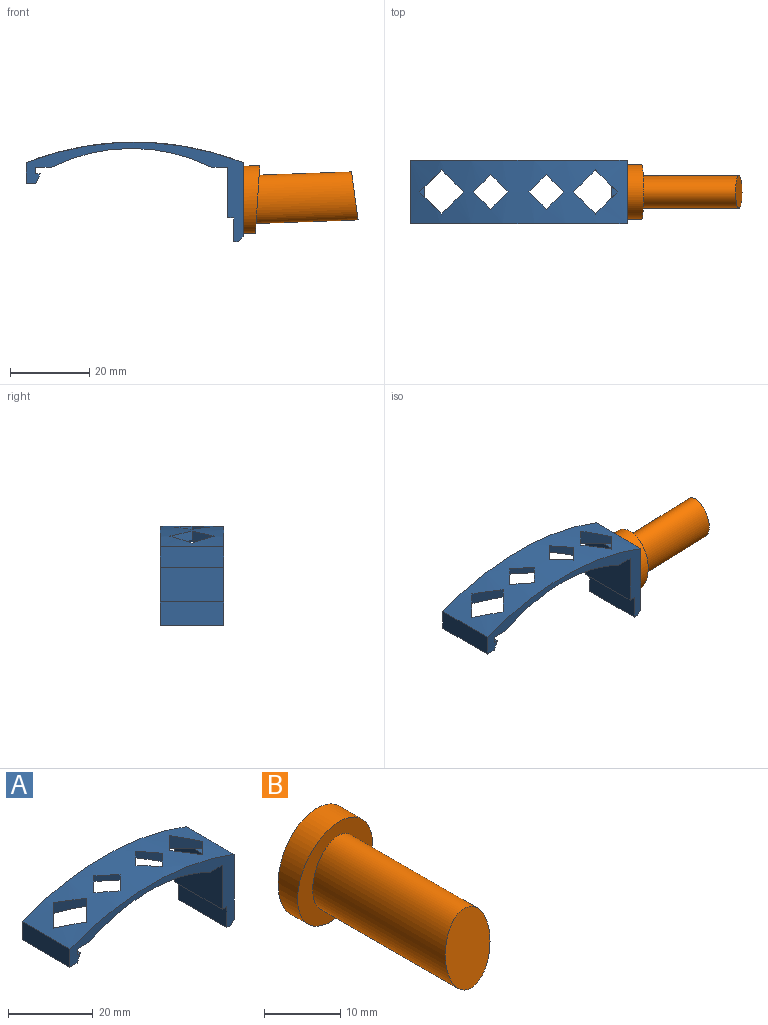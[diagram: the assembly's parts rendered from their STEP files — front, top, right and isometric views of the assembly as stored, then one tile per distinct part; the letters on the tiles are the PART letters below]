
ASSEMBLY  parts=2 mates=1
PART A: 36 faces, bbox 54.9x16x25.2 mm
  f0: plane 6.5x4mm, normal (0,0,-1), area 18mm2, adj f5,f6,f17,f28
  f1: plane 6.5x4mm, normal (0,0,-1), area 18mm2, adj f5,f6,f16,f27
  f2: plane 8x4mm, normal (0,0,-1), area 24mm2, adj f5,f15,f16,f31
  f3: plane 8x4mm, normal (0,0,-1), area 24mm2, adj f5,f15,f17,f34
  f4: cylinder r=75.05mm len=54.9mm, axis (0,1,0), area 691.5mm2, adj f10,f11,f16,f17,f18,f19,f20,f21
  f5: cylinder r=45.33mm len=40.6mm, axis (0,1,0), area 508.8mm2, adj f0,f1,f2,f3,f16,f17,f18,f19
  f6: plane 16x12.8mm, normal (-1,0,0), area 204.8mm2, adj f0,f1,f7,f16,f17,f30
  f7: plane 16x1.5mm, normal (0,0,-1), area 24mm2, adj f6,f8,f16,f17
  f8: plane 16x6mm, normal (-1,0,0), area 96mm2, adj f7,f9,f16,f17
  f9: plane 16x1.2mm, normal (0,0,-1), area 19.2mm2, adj f8,f16,f17,f35
  f10: plane 18.8x16mm, normal (1,0,0), area 300.8mm2, adj f4,f16,f17,f35
  f11: plane 16x5.25mm, normal (-1,0,0), area 84mm2, adj f4,f12,f16,f17
  f12: plane 16x2.4mm, normal (0,0,-1), area 38.4mm2, adj f11,f13,f16,f17
  f13: plane 16x2.4mm, normal (0.89,0,-0.45), area 42.9mm2, adj f12,f14,f16,f17
  f14: plane 16x1.2mm, normal (0,0,1), area 19.2mm2, adj f13,f15,f16,f17
  f15: plane 16x1.65mm, normal (1,0,0), area 26.4mm2, adj f2,f3,f14,f16,f17
  f16: plane 54.9x25.2mm, normal (0,-1,0), area 201mm2, adj f1,f2,f4,f5,f6,f7,f8,f9
  f17: plane 54.9x25.2mm, normal (0,1,0), area 201mm2, adj f0,f3,f4,f5,f6,f7,f8,f9
  f18: plane 4.41x4.41mm, normal (-0.71,0.71,0), area 10.2mm2, adj f4,f5,f19,f21
  f19: plane 4.41x4.41mm, normal (-0.71,-0.71,0), area 10.2mm2, adj f4,f5,f18,f20
  f20: plane 4.41x4.41mm, normal (0.71,-0.71,0), area 11.4mm2, adj f4,f5,f19,f21
  f21: plane 4.41x4.41mm, normal (0.71,0.71,0), area 11.4mm2, adj f4,f5,f18,f20
  f22: plane 4.41x4.41mm, normal (-0.71,0.71,0), area 13.4mm2, adj f4,f5,f23,f25
  f23: plane 4.41x4.41mm, normal (-0.71,-0.71,0), area 13.4mm2, adj f4,f5,f22,f24
  f24: plane 4.41x4.41mm, normal (0.71,-0.71,0), area 11.2mm2, adj f4,f5,f23,f25
  f25: plane 4.41x4.41mm, normal (0.71,0.71,0), area 11.2mm2, adj f4,f5,f22,f24
  f26: plane 5.6x5.6mm, normal (0.71,0.71,0), area 25.5mm2, adj f4,f5,f27,f29
  f27: plane 5.6x5.6mm, normal (-0.71,0.71,0), area 23.8mm2, adj f1,f4,f5,f26,f28,f30
  f28: plane 5.6x5.6mm, normal (-0.71,-0.71,0), area 23.8mm2, adj f0,f4,f5,f27,f29,f30
  f29: plane 5.6x5.6mm, normal (0.71,-0.71,0), area 25.5mm2, adj f4,f5,f26,f28
  f30: plane 3x1.5mm, normal (0,0,1), area 2.3mm2, adj f6,f27,f28
  f31: plane 5.61x5.61mm, normal (0.71,0.71,0), area 22.9mm2, adj f2,f4,f5,f32,f34
  f32: plane 5.6x5.6mm, normal (-0.71,0.71,0), area 20.8mm2, adj f4,f5,f31,f33
  f33: plane 5.6x5.6mm, normal (-0.71,-0.71,0), area 20.8mm2, adj f4,f5,f32,f34
  f34: plane 5.61x5.61mm, normal (0.71,-0.71,0), area 22.9mm2, adj f3,f4,f5,f31,f33
  f35: plane 16x1.2mm, normal (0.71,0,-0.71), area 27.2mm2, adj f9,f10,f16,f17
PART B: 5 faces, bbox 13.8x29.2x17 mm
  f0: extruded ~25.82x12.2mm, area 795.9mm2, adj f1,f2
  f1: plane 12.2x8.2mm, normal (0,-1,0.1), area 79mm2, adj f0
  f2: plane 17x13.81mm, normal (0,-1,-0.1), area 106.3mm2, adj f0,f3
  f3: extruded ~17x13.8mm, area 178.5mm2, adj f2,f4
  f4: plane 17x13.81mm, normal (0,1,0.03), area 184.5mm2, adj f3
PLACE A t=(-21.06,0.13,2.96)mm
PLACE B rot(axis=(-0.02,-0.02,1),90deg) t=(47.41,0.13,-4.69)mm
MATE fastened B.f4 <-> A.f10  axis (1,0,0) through (31.44,0.13,-5.24)mm
